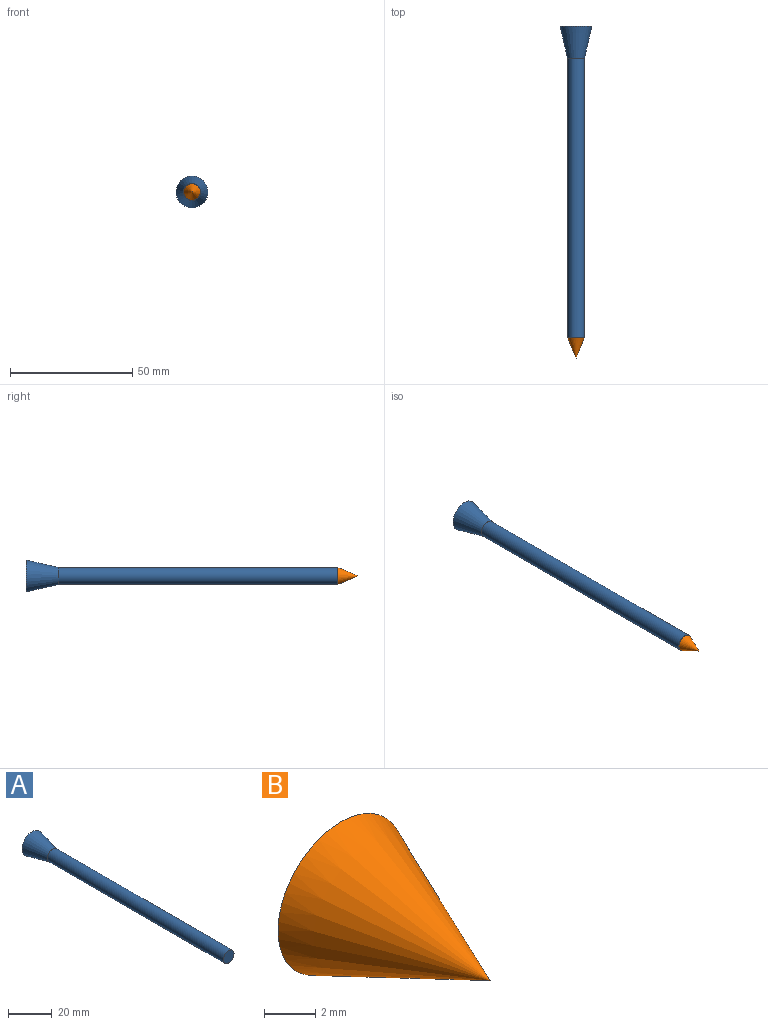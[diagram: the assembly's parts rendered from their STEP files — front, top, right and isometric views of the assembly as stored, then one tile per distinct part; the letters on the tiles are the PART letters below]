
ASSEMBLY  parts=2 mates=1
PART A: 6 faces, bbox 13x127.4x13 mm
  f0: plane 13x13mm, normal (0,1,0), area 25.2mm2, adj f1,f3
  f1: cone r=3.45mm half-angle=12.8deg, axis (0,1,0), area 429.5mm2, adj f0,f4
  f2: cone r=0mm half-angle=59deg, axis (0,1,0), area 125.4mm2, adj f3
  f3: cylinder r=5.85mm len=11.7mm, axis (0,1,0), area 25.7mm2, adj f0,f2
  f4: cylinder r=3.45mm len=114mm, axis (0,1,0), area 2469.8mm2, adj f1,f5
  f5: plane 6.9x6.9mm, normal (0,-1,0), area 37.4mm2, adj f4
PART B: 2 faces, bbox 6.9x8.2x6.9 mm
  f0: plane 6.9x6.9mm, normal (0,1,0), area 37.4mm2, adj f1
  f1: cone r=3.45mm half-angle=22.8deg, axis (0,1,0), area 96.4mm2, adj f0
PLACE A at identity
PLACE B t=(0,-127.4,0)mm
MATE fastened B.f1 <-> A.f1  axis (0,1,0) through (0,-127.4,0)mm
